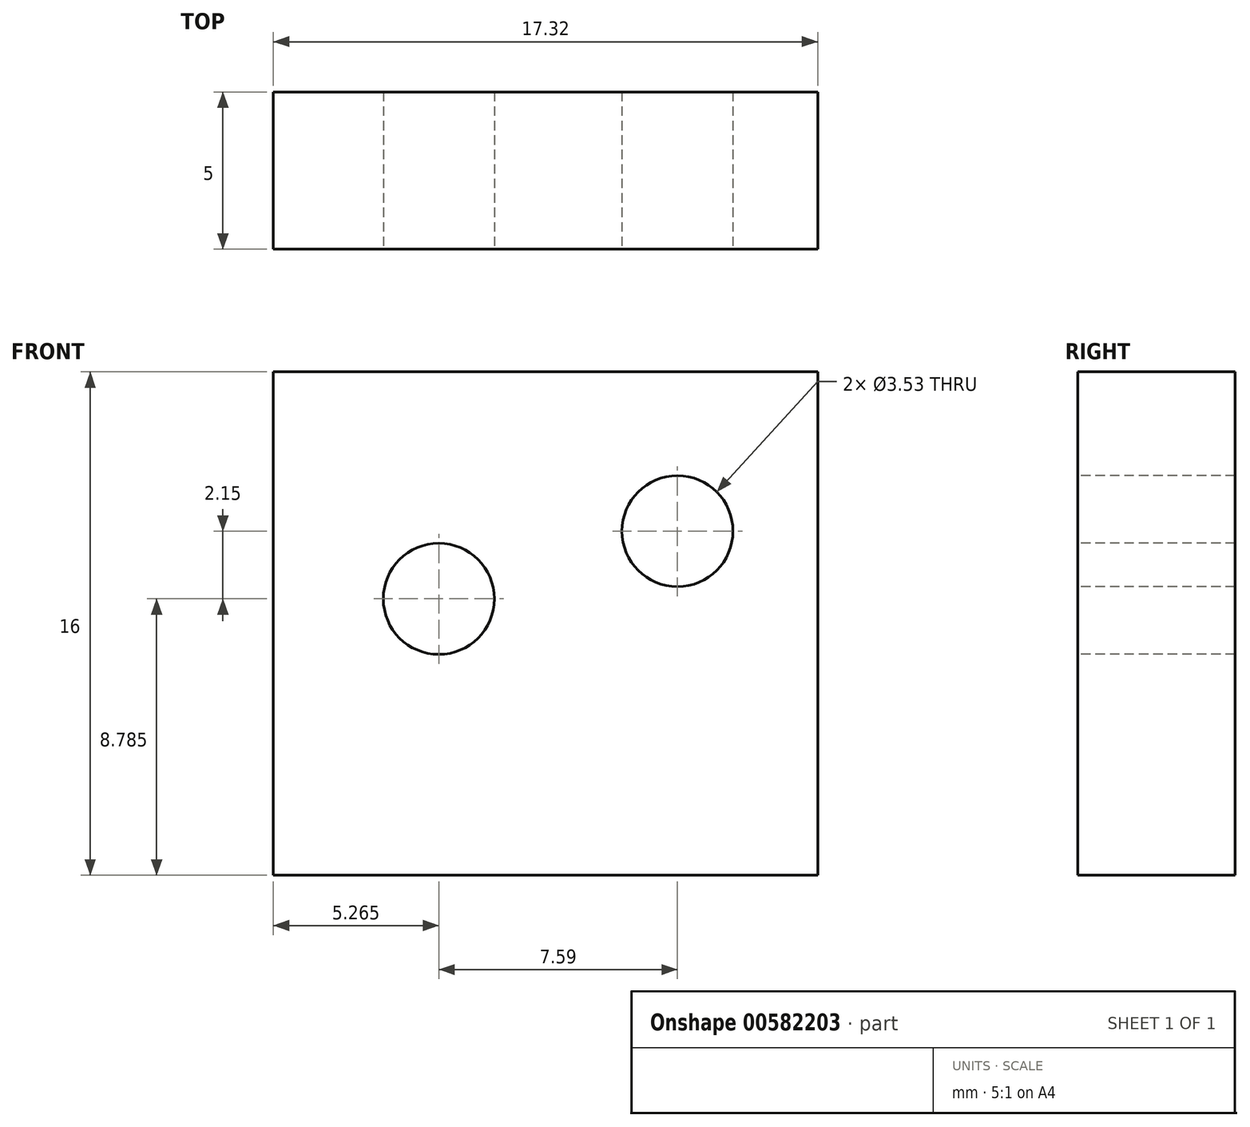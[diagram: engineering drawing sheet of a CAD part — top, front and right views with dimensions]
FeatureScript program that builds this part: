
annotation { "Feature Type Name" : "Feature", "Feature Type Description" : "" }
export const myFeature = defineFeature(function(context is Context, id is Id, definition is map)
    precondition{}
    {
        {
            var Q0;
            Q0=qCreatedBy(makeId("Front.planeOp"),FACE);
            var sketch = newSketch(context, id + "F0", { "sketchPlane" : qUnion([Q0])});
            skLineSegment(sketch, "E0.bottom", {"start": v(0, 0) * mm, "end": v(17.32, 0) * mm});
            skLineSegment(sketch, "E0.top", {"start": v(0, 16) * mm, "end": v(17.32, 16) * mm});
            skLineSegment(sketch, "E0.left", {"start": v(0, 0) * mm, "end": v(0, 16) * mm});
            skLineSegment(sketch, "E0.right", {"start": v(17.32, 0) * mm, "end": v(17.32, 16) * mm});
            skSolve(sketch);
        }
        {
            var Q0;
            Q0=makeQuery(id+"F0.imprint","IMPRINT",FACE,{"disambiguationData":[TD([[makeQuery(id+"F0.imprint","IMPRINT",EDGE,{"derivedFrom":sQuery(id+"F0.wireOp",EDGE,"E0.bottom")}),1.0]])]});
            extrude(context, id + "F1", {"entities" : qUnion([Q0]), "depth" : 5 * mm, "offsetDistance" : 25 * mm});
        }
        {
            var Q0;
            Q0=makeQuery(id+"F1.opExtrude","CAP_FACE",FACE,{"disambiguationData":[OSD([sQuery(id+"F0.wireOp",EDGE,"E0.bottom"),sQuery(id+"F0.wireOp",EDGE,"E0.top"),sQuery(id+"F0.wireOp",EDGE,"E0.left"),sQuery(id+"F0.wireOp",EDGE,"E0.right")])],"isStart":false});
            var sketch = newSketch(context, id + "F2", { "sketchPlane" : qUnion([Q0])});
            skCircle(sketch, "E1", {"center": v(12.86, 10.94) * mm, "radius": 1.76 * mm});
            skSolve(sketch);
        }
        {
            var Q0;
            Q0=makeQuery(id+"F2.imprint","IMPRINT",FACE,{"disambiguationData":[TD([[makeQuery(id+"F2.imprint","IMPRINT",EDGE,{"derivedFrom":sQuery(id+"F2.wireOp",EDGE,"E1")}),-1.0]])]});
            var sketch = newSketch(context, id + "F3", { "sketchPlane" : qUnion([Q0])});
            skCircle(sketch, "E2", {"center": v(5.26, 8.79) * mm, "radius": 1.76 * mm});
            skSolve(sketch);
        }
        {
            var Q0;
            Q0=makeQuery(id+"F2.imprint","IMPRINT",FACE,{"disambiguationData":[TD([[makeQuery(id+"F2.imprint","IMPRINT",EDGE,{"derivedFrom":sQuery(id+"F2.wireOp",EDGE,"E1")}),1.0]])]});
            var Q1;
            Q1=makeQuery(id+"F1.opExtrude","CAP_FACE",FACE,{"disambiguationData":[OSD([sQuery(id+"F0.wireOp",EDGE,"E0.bottom"),sQuery(id+"F0.wireOp",EDGE,"E0.top"),sQuery(id+"F0.wireOp",EDGE,"E0.left"),sQuery(id+"F0.wireOp",EDGE,"E0.right")])],"isStart":true});
            extrude(context, id + "F4", {"entities" : qUnion([Q0]), "operationType" : NewBodyOperationType.REMOVE, "endBound" : BoundingType.UP_TO_SURFACE, "oppositeDirection" : true, "depth" : 25 * mm, "endBoundEntityFace" : qUnion([Q1]), "offsetDistance" : 25 * mm});
        }
        {
            var Q0;
            Q0=makeQuery(id+"F3.imprint","IMPRINT",FACE,{"disambiguationData":[TD([[makeQuery(id+"F3.imprint","IMPRINT",EDGE,{"derivedFrom":sQuery(id+"F3.wireOp",EDGE,"E2")}),1.0]])]});
            var Q1;
            Q1=makeQuery(id+"F1.opExtrude","CAP_FACE",FACE,{"disambiguationData":[OSD([sQuery(id+"F0.wireOp",EDGE,"E0.bottom"),sQuery(id+"F0.wireOp",EDGE,"E0.top"),sQuery(id+"F0.wireOp",EDGE,"E0.left"),sQuery(id+"F0.wireOp",EDGE,"E0.right")])],"isStart":true});
            extrude(context, id + "F5", {"entities" : qUnion([Q0]), "operationType" : NewBodyOperationType.REMOVE, "endBound" : BoundingType.UP_TO_SURFACE, "oppositeDirection" : true, "depth" : 25 * mm, "endBoundEntityFace" : qUnion([Q1]), "offsetDistance" : 25 * mm});
        }
    });
